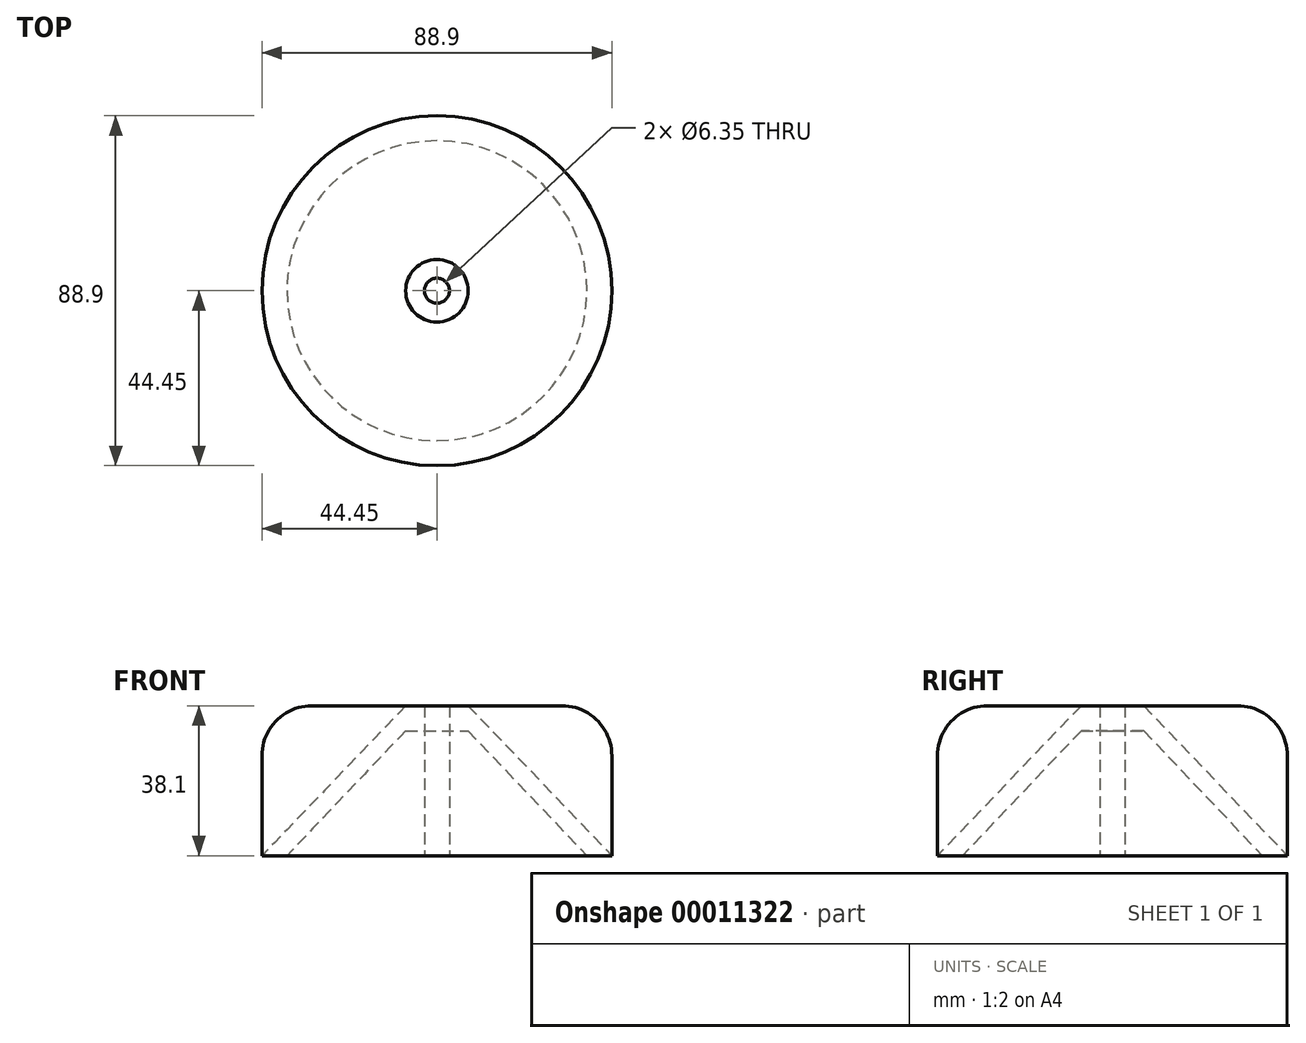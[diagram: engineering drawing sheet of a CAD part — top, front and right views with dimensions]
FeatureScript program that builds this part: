
annotation { "Feature Type Name" : "Feature", "Feature Type Description" : "" }
export const myFeature = defineFeature(function(context is Context, id is Id, definition is map)
    precondition{}
    {
        {
            var Q0;
            Q0=qCreatedBy(makeId("Front.planeOp"),FACE);
            var sketch = newSketch(context, id + "F0", { "sketchPlane" : qUnion([Q0])});
            skLineSegment(sketch, "E0", {"start": v(7.94, 31.75) * mm, "end": v(7.94, 38.1) * mm});
            skLineSegment(sketch, "E1", {"start": v(7.94, 38.1) * mm, "end": v(44.45, 0) * mm});
            skLineSegment(sketch, "E2", {"start": v(44.45, 0) * mm, "end": v(38.1, 0) * mm});
            skLineSegment(sketch, "E3", {"start": v(38.1, 0) * mm, "end": v(7.94, 31.75) * mm});
            skLineSegment(sketch, "E4.bottom", {"start": v(7.94, 31.75) * mm, "end": v(3.17, 31.75) * mm});
            skLineSegment(sketch, "E4.top", {"start": v(7.94, 38.1) * mm, "end": v(3.17, 38.1) * mm});
            skLineSegment(sketch, "E4.right", {"start": v(3.17, 31.75) * mm, "end": v(3.17, 38.1) * mm});
            skLineSegment(sketch, "E5", {"start": v(0, 0) * mm, "end": v(0, 38.1) * mm, "construction": true});
            skLineSegment(sketch, "E6.bottom", {"start": v(3.17, 38.1) * mm, "end": v(44.45, 38.1) * mm});
            skLineSegment(sketch, "E6.top", {"start": v(3.17, 0) * mm, "end": v(44.45, 0) * mm});
            skLineSegment(sketch, "E6.left", {"start": v(3.17, 38.1) * mm, "end": v(3.17, 0) * mm});
            skLineSegment(sketch, "E6.right", {"start": v(44.45, 38.1) * mm, "end": v(44.45, 0) * mm});
            skSolve(sketch);
        }
        {
            var Q0;
            Q0=makeQuery(id+"F0.imprint","IMPRINT",FACE,{"disambiguationData":[TD([[makeQuery(id+"F0.imprint","IMPRINT",EDGE,{"derivedFrom":sQuery(id+"F0.wireOp",EDGE,"E1")}),-1.0]])]});
            var Q1;
            Q1=makeQuery(id+"F0.imprint","IMPRINT",FACE,{"disambiguationData":[TD([[makeQuery(id+"F0.imprint","IMPRINT",EDGE,{"derivedFrom":sQuery(id+"F0.wireOp",EDGE,"E4.bottom")}),-1.0]])]});
            var Q2;
            {var subQ4=sQuery(id+"F0.wireOp",EDGE,"E3");Q2=makeQuery(id+"F0.imprint","IMPRINT",FACE,{"disambiguationData":[TD([[makeQuery(id+"F0.imprint","IMPRINT",EDGE,{"derivedFrom":subQ4}),1.0]])]});}
            var Q3;
            {var subQ2=sQuery(id+"F0.wireOp",EDGE,"E1");Q3=makeQuery(id+"F0.imprint","IMPRINT",FACE,{"disambiguationData":[TD([[makeQuery(id+"F0.imprint","IMPRINT",EDGE,{"derivedFrom":subQ2}),1.0]])]});}
            var Q4;
            Q4=sQuery(id+"F0.wireOp",EDGE,"E5");
            revolve(context, id + "F1", {"entities" : qUnion([Q0, Q1, Q2, Q3]), "axis" : qUnion([Q4]), "revolveType" : RevolveType.FULL});
        }
        {
            var Q0;
            Q0=makeQuery(id+"F1.opRevolve","SWEPT_EDGE",EDGE,{"disambiguationData":[OSD([sQuery(id+"F0.wireOp",EDGE,"E6.bottom"),sQuery(id+"F0.wireOp",EDGE,"E6.right")])]});
            fillet(context, id + "F2", {"entities" : qUnion([Q0]), "radius" : 12.7 * mm, "tangentPropagation" : true, "allowEdgeOverflow" : false});
        }
        {
            var Q0;
            {var subQ2=sQuery(id+"F0.wireOp",EDGE,"E1");Q0=makeQuery(id+"F0.imprint","IMPRINT",FACE,{"disambiguationData":[TD([[makeQuery(id+"F0.imprint","IMPRINT",EDGE,{"derivedFrom":subQ2}),-1.0]])]});}
            var Q1;
            {var subQ3=sQuery(id+"F0.wireOp",EDGE,"E4.bottom");Q1=makeQuery(id+"F0.imprint","IMPRINT",FACE,{"disambiguationData":[TD([[makeQuery(id+"F0.imprint","IMPRINT",EDGE,{"derivedFrom":subQ3}),-1.0]])]});}
            var Q2;
            Q2=sQuery(id+"F0.wireOp",EDGE,"E5");
            revolve(context, id + "F3", {"entities" : qUnion([Q0, Q1]), "axis" : qUnion([Q2]), "revolveType" : RevolveType.FULL});
        }
    });
